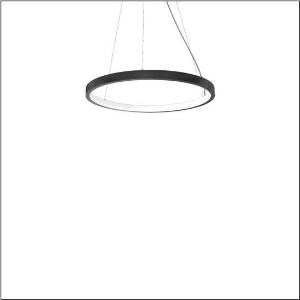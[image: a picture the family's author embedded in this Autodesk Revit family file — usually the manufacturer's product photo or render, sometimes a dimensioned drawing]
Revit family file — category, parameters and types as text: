
# Revit family: silica_r__21_ring-i_5pjbi2d1104a_14c4
name_source: partatom
category: Lighting Fixtures
units: mm (PartAtom-declared; Revit-internal decimal feet)

## family parameters
Cut with Voids When Loaded = No
Host = Face
Light Source = No
Part Type = Normal
Room Calculation Point = No
Round Connector Dimension = Use Diameter
Shared = No

## types (1)
- Silica® 21 Ring-I (1 x LED, 4800 lm, 80 W, 3000K)
    Apparent Load = 80 VA
    CIE Flux Codes = 22 48 76 50 101
    Color Rendering = 80
    Color Temperature = 3000K
    Default Elevation = 1800 mm
    Description = Silica® 21 Ring-I, suspended luminaire, of PMMA, frosted, light emission: inner ring side luminous distribution, primary light characteristic: symmetric, installation type: suspended mounting, LED, rated luminous flux: 4.800lm, luminous efficacy: 60lm/W, light colour: 830, colour temperature: 3000K, with terminal, 5-pole, mains connection: 230V, AC/DC, 0/50..60Hz, rated input power: 80W, housing, of extruded aluminium section, jet black (RAL 9005), diameter: 805mm, ceiling canopy, jet black (RAL 9005), protection rating (lamp compartment): IP40, insulation class (complete): insulation class I (protective earthing), certification: CE, impact resistance: IK02, permissible operating ambient temperature: 0..+35°C, packaging unit: 1 piece
    Height = 48 mm  [stored 0.15748 ft]
    Lamp = 1 x LED
    Lamp Light Flux = 4800 lm
    Lamp Power = 80 W
    Lamp count = 1
    Length = 805 mm
    Luminous efficacy = 60 lm/W
    Manufacturer = Siteco
    ModVariant = No
    Model = 5PJBI2D1104A
    Mounting Place = Ceiling
    Mounting Type = Pendant
    Number of Poles = 1
    OnlyDefault = Yes
    Power Factor = 1
    Product Name = Silica® 21 Ring-I
    Product group = suspended luminaire
    ProductGroupID = 904
    Protection Class = Protection class I
    Protection Degree = Degree of protection
    RLX_Detail_Level = 1
    RLX_Emergency_Light_Flux = 0 lm
    RLX_Emergency_Type = 0
    RLX_Emergency_Type_DB = No
    RlxData = <blob elided: 13909 chars, md5=5731a750>
    Socket = socket
    Standby Power = 0 W
    System Light Flux = 4800 lm
    System Power = 80 W
    Type Comments = Product without accessories
    Type Image = l_1258365.jpg
    URL = http://relux.com
    VarID = ---
    Voltage = 0 V
    Weight = 0.00 kg
    Width = 0 mm  [stored 0 ft]

note: [stored X ft] marks values corroborated as IEEE doubles in the binary element streams (Revit-internal decimal feet)

## geometry (parser evidence)
native form markers: Sweep x14
no freeform markers — native parametric forms only
